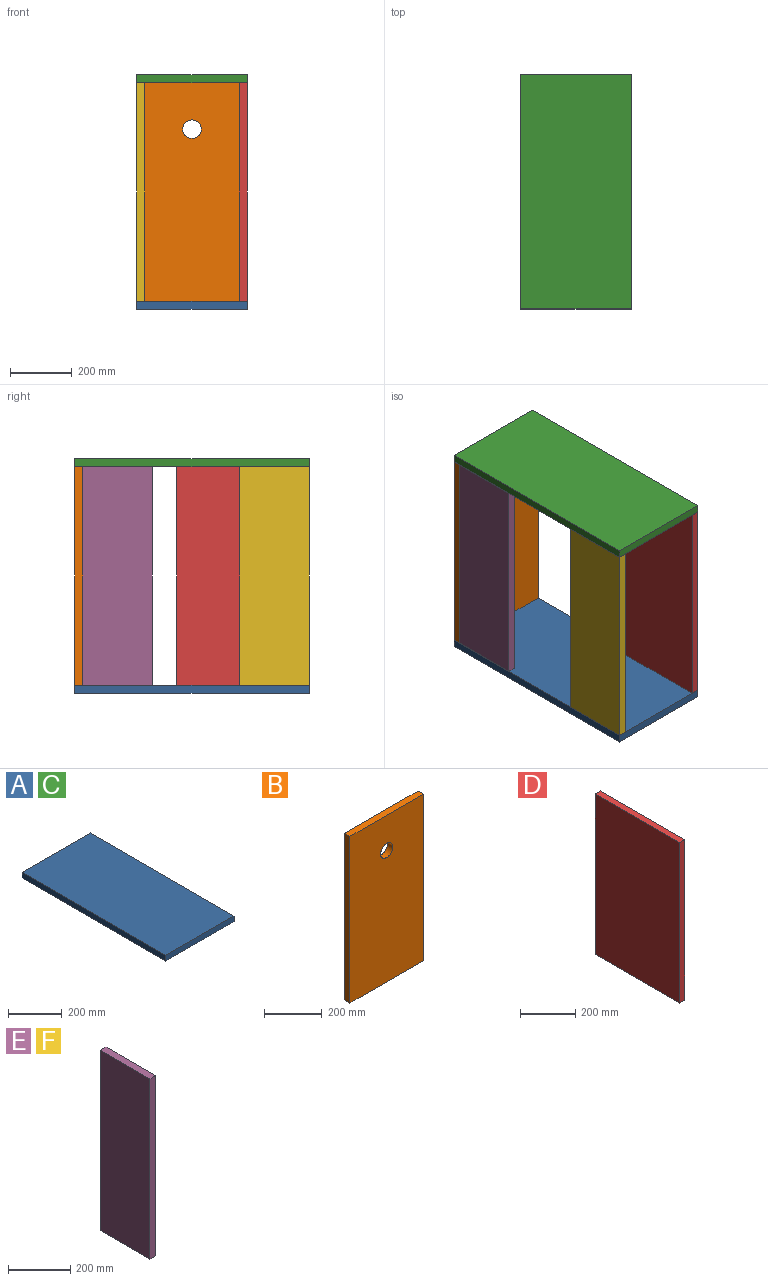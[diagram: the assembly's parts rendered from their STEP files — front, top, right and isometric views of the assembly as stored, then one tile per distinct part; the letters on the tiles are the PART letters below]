
ASSEMBLY  parts=6 mates=5
PART A: 6 faces, bbox 360x760x26 mm
  f0: plane 760x26mm, normal (1,0,0), area 19760mm2, adj f1,f3,f4,f5
  f1: plane 360x26mm, normal (0,1,0), area 9360mm2, adj f0,f2,f4,f5
  f2: plane 760x26mm, normal (-1,0,0), area 19760mm2, adj f1,f3,f4,f5
  f3: plane 360x26mm, normal (0,-1,0), area 9360mm2, adj f0,f2,f4,f5
  f4: plane 760x360mm, normal (0,0,1), area 273600mm2, adj f0,f1,f2,f3
  f5: plane 760x360mm, normal (0,0,-1), area 273600mm2, adj f0,f1,f2,f3
PART B: 7 faces, bbox 360x26x708 mm
  f0: plane 708x26mm, normal (-1,0,0), area 18408mm2, adj f1,f3,f5,f6
  f1: plane 360x26mm, normal (0,0,-1), area 9360mm2, adj f0,f2,f5,f6
  f2: plane 708x26mm, normal (1,0,0), area 18408mm2, adj f1,f3,f5,f6
  f3: plane 360x26mm, normal (0,0,1), area 9360mm2, adj f0,f2,f5,f6
  f4: cylinder r=30mm len=60mm, axis (0,1,0), area 4900.9mm2, adj f5,f6
  f5: plane 708x360mm, normal (0,-1,0), area 252052.6mm2, adj f0,f1,f2,f3,f4
  f6: plane 708x360mm, normal (0,1,0), area 252052.6mm2, adj f0,f1,f2,f3,f4
PART C: same geometry as A
PART D: 6 faces, bbox 26x430x708 mm
  f0: plane 708x26mm, normal (0,1,0), area 18408mm2, adj f1,f3,f4,f5
  f1: plane 430x26mm, normal (0,0,1), area 11180mm2, adj f0,f2,f4,f5
  f2: plane 708x26mm, normal (0,-1,0), area 18408mm2, adj f1,f3,f4,f5
  f3: plane 430x26mm, normal (0,0,-1), area 11180mm2, adj f0,f2,f4,f5
  f4: plane 708x430mm, normal (1,0,0), area 304440mm2, adj f0,f1,f2,f3
  f5: plane 708x430mm, normal (-1,0,0), area 304440mm2, adj f0,f1,f2,f3
PART E: 6 faces, bbox 26x225x708 mm
  f0: plane 708x26mm, normal (0,1,0), area 18408mm2, adj f1,f3,f4,f5
  f1: plane 225x26mm, normal (0,0,1), area 5850mm2, adj f0,f2,f4,f5
  f2: plane 708x26mm, normal (0,-1,0), area 18408mm2, adj f1,f3,f4,f5
  f3: plane 225x26mm, normal (0,0,-1), area 5850mm2, adj f0,f2,f4,f5
  f4: plane 708x225mm, normal (1,0,0), area 159300mm2, adj f0,f1,f2,f3
  f5: plane 708x225mm, normal (-1,0,0), area 159300mm2, adj f0,f1,f2,f3
PART F: same geometry as E
PLACE A t=(146.84,-109.82,-121.4)mm
PLACE B t=(146.84,270.18,258.6)mm
PLACE C t=(146.84,-109.82,612.6)mm
PLACE D t=(300.84,-274.82,258.6)mm
PLACE E t=(-33.16,131.68,258.6)mm
PLACE F t=(-33.16,-377.32,258.6)mm
MATE fastened D.f1 <-> C.f5  axis (0,0,1) through (326.84,-489.82,612.6)mm
MATE fastened F.f1 <-> C.f5  axis (0,0,1) through (-33.16,-489.82,612.6)mm
MATE fastened A.f4 <-> B.f1  axis (0,0,1) through (-33.16,270.18,-95.4)mm
MATE fastened C.f5 <-> B.f3  axis (0,0,-1) through (-33.16,270.18,612.6)mm
MATE fastened E.f0 <-> B.f5  axis (0,1,0) through (-33.16,244.18,612.6)mm
